# Revit family: 304_F386_2___B
name_source: partatom
category: Pipe Accessories
units: mm (PartAtom-declared; Revit-internal decimal feet)

## family parameters
Always vertical = Yes
Cut with Voids When Loaded = No
Part Type = Valve - Breaks Into
Round Connector Dimension = Use Diameter
Shared = No
Work Plane-Based = No

## types (3) — shared parameters
CAT0 = Yes
Description = AHU-Wafer - Automatic Balancing Valve - Pre-Set Cartridge
L = 175 mm
L1 = 44 mm
L2D = 174 mm
L2D_Min = 3048 mm  [stored 10 ft]
LL = 87 mm
Manufacturer = FlowCon
QmdConnectorList = 301;D;302;D
URL = http://flowcon.com
magiPartTypeId = 304
magiProductFamilyId = F386.2.*.B
zero-valued in all types: MC_Default_elevation

## per-type parameters (varying)
| type | D | H1 | R2 | W2D |
| F386.2.L.B-50 | 50 mm | 140 mm  [stored 0.459318 ft] | 54 mm | 50 mm  [stored 0.164042 ft] |
| F386.2.M.B-80 | 80 mm | 144 mm  [stored 0.472441 ft] | 59 mm  [stored 0.19357 ft] | 80 mm  [stored 0.262467 ft] |
| F386.2.M.B-65 | 65 mm | 144 mm  [stored 0.472441 ft] | 59 mm  [stored 0.19357 ft] | 65 mm  [stored 0.213255 ft] |

note: column(s) folded — value = type name in every type: magiProductCode, magiProductId

note: [stored X ft] marks values corroborated as IEEE doubles in the binary element streams (Revit-internal decimal feet)

## geometry (parser evidence)
native form markers: Sweep x2
no freeform markers — native parametric forms only
